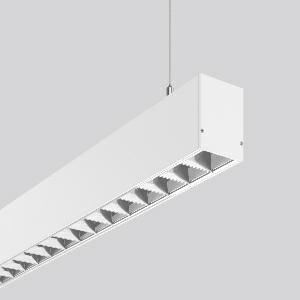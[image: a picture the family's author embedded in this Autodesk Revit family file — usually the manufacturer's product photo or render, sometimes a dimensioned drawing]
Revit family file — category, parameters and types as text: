
# Revit family: less_is_more_50_312341_002_1_fd4c
name_source: partatom
category: Lighting Fixtures
units: mm (PartAtom-declared; Revit-internal decimal feet)

## family parameters
Cut with Voids When Loaded = No
Host = Face
Light Source = No
Part Type = Normal
Room Calculation Point = No
Round Connector Dimension = Use Diameter
Shared = No

## types (1)
- LESS IS MORE 50 (1 x LED Modul 840, 4200 lm, 4000)
    Apparent Load = 35 VA
    CIE Flux Codes = 95 100 100 63 100
    Color Rendering = 80
    Color Temperature = 4000
    Default Elevation = 1800 mm
    Description = Series: LESS IS MORE 50
Linear pendant luminaire for aesthetically sophisticated lighting. Housing: extruded aluminium profile, powder-coated. End cap aluminium powder-coated. Canopy made of aluminium, powder-coated. Alea optical system: Reflector structure (ABS, Aluminium-coated, highly polished) with integrated diffuser made of non-yellowing plastic (PMMA) opal for glare-free light at the workstation (screen-compliant according to EN 12464-1). Direct 65%, indirect 35% light emission. Suitable for pendant. 2-point steel cable suspension freely positionable and infinitely height-adjustable. Special lengths available on request. LED unit with integrated converter interchangeable and removable. Suitable for through-wiring. With sensors or as a safety luminaire on request. 
Colour: traffic white, matt (RAL 9016)
Length: 847 mm
Width: 57 mm
Height: 75 mm
Suspension length: 2000 mm
Lamp: LED
Socket: without socket
Colour temperature: 4000K
Colour rendering index (CRI): 80
Light source: LED
Socket lamp2: Without base
Colour temperature: 4000K
System power: 35 W
Rated luminous flux: 4200 lm
Luminous efficiency: 120 lm/W
Control gear: Regulated power supply
Control gear: Regulated power supply
Protection class: I
Type of protection: IP 20
    Height = 75 mm
    Lamp = 1 x LED Modul 840
    Lamp Light Flux = 4200 lm
    Lamp count = 1
    Length = 847 mm
    Lifetime = 50000 h
    Luminous efficacy = 120 lm/W
    Manufacturer = RZB
    ModVariant = No
    Model = 312341.002.1
    Mounting Place = Ceiling
    Mounting Type = Pendant
    Number of Poles = 1
    OnlyDefault = Yes
    Power Factor = 1
    Product Name = LESS IS MORE 50
    Product group = Pendant LED linear luminaires
    ProductGroupID = 907
    Protection Class = Protection class I
    Protection Degree = IP 20
    RLX_Detail_Level = 1
    RLX_Emergency_Light_Flux = 0 lm
    RLX_Emergency_Type = 0
    RLX_Emergency_Type_DB = No
    RlxData = <blob elided: 37477 chars, md5=4446cf0a>
    Socket = socket
    Standby Power = 0 W
    System Light Flux = 4200 lm
    System Power = 35 W
    Type Comments = Product without accessories
    Type Image = 312342.002.jpg
    URL = http://relux.com
    VarID = ---
    Voltage = 230 V
    Voltage Range = 220-240 V
    Weight = 0.00 kg
    Width = 57 mm

## geometry (parser evidence)
native form markers: Blend x4, Sweep x13
no freeform markers — native parametric forms only
